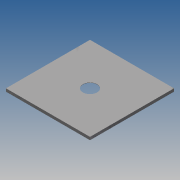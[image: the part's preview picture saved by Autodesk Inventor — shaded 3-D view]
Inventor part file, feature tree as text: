
AUTODESK INVENTOR PART (.ipt)
format: ipt  version: 2014 SP1 (Build 180222100, 222)  size: 94,208 bytes
history: native  units: in
note: dims shown in document units (in); Inventor stores cm internally (conversion verified against a paired STEP export)
features: extrude x3, sketch x3
ambient origin geometry x8: Origin, YZ Plane, XZ Plane, XY Plane, X Axis, Y Axis, Z Axis, Center Point
bodies: Solid1 (feature_tree)
feature tree (6):
  extrude  "Extrusion1"  Depth=34.252in
  extrude  "Extrusion2"  Depth=0.3937in
  extrude  "Extrusion3"  Depth=1.0827in
  sketch  "Sketch1"  dims[d0=34.252in d1=34.252in]
  sketch  "Sketch2"  dims[d2=1.1811in d3=0.0in d4=0.3937in]
  sketch  "Sketch3"  dims[d5=1.0827in d6=0.0in d7=5.8in d8=1.0in d9=0.0in]
